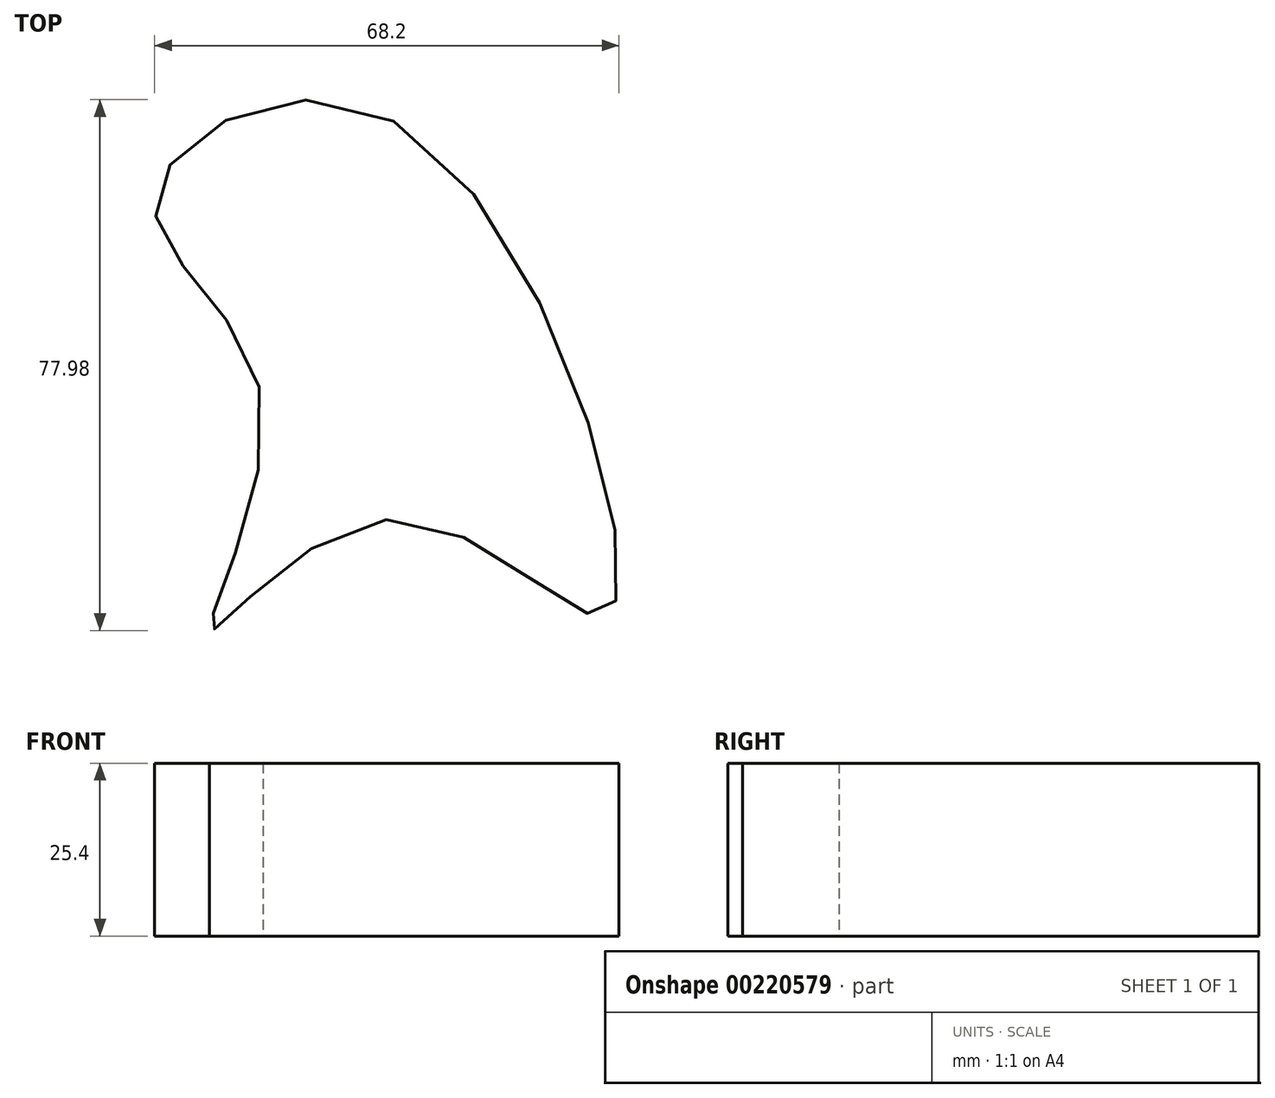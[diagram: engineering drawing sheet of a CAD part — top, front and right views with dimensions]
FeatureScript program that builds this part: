
annotation { "Feature Type Name" : "Feature", "Feature Type Description" : "" }
export const myFeature = defineFeature(function(context is Context, id is Id, definition is map)
    precondition{}
    {
        {
            var Q0;
            Q0=qCreatedBy(makeId("Top.planeOp"),FACE);
            var sketch = newSketch(context, id + "F0", { "sketchPlane" : qUnion([Q0])});
            skFitSpline(sketch, "E0", {"points": [v(0, 40.57) * mm, v(-35.01, 29.09) * mm, v(-19.45, 0) * mm, v(-26.86, -34.27) * mm, v(0, -17.97) * mm, v(31.68, -31.68) * mm, v(0, 40.57) * mm]});
            skSolve(sketch);
        }
        {
            var Q0;
            Q0=makeQuery(id+"F0.imprint","IMPRINT",FACE,{"disambiguationData":[TD([[makeQuery(id+"F0.imprint","IMPRINT",EDGE,{"derivedFrom":sQuery(id+"F0.wireOp",EDGE,"E0")}),1.0]])]});
            extrude(context, id + "F1", {"entities" : qUnion([Q0]), "depth" : 25.4 * mm});
        }
    });
